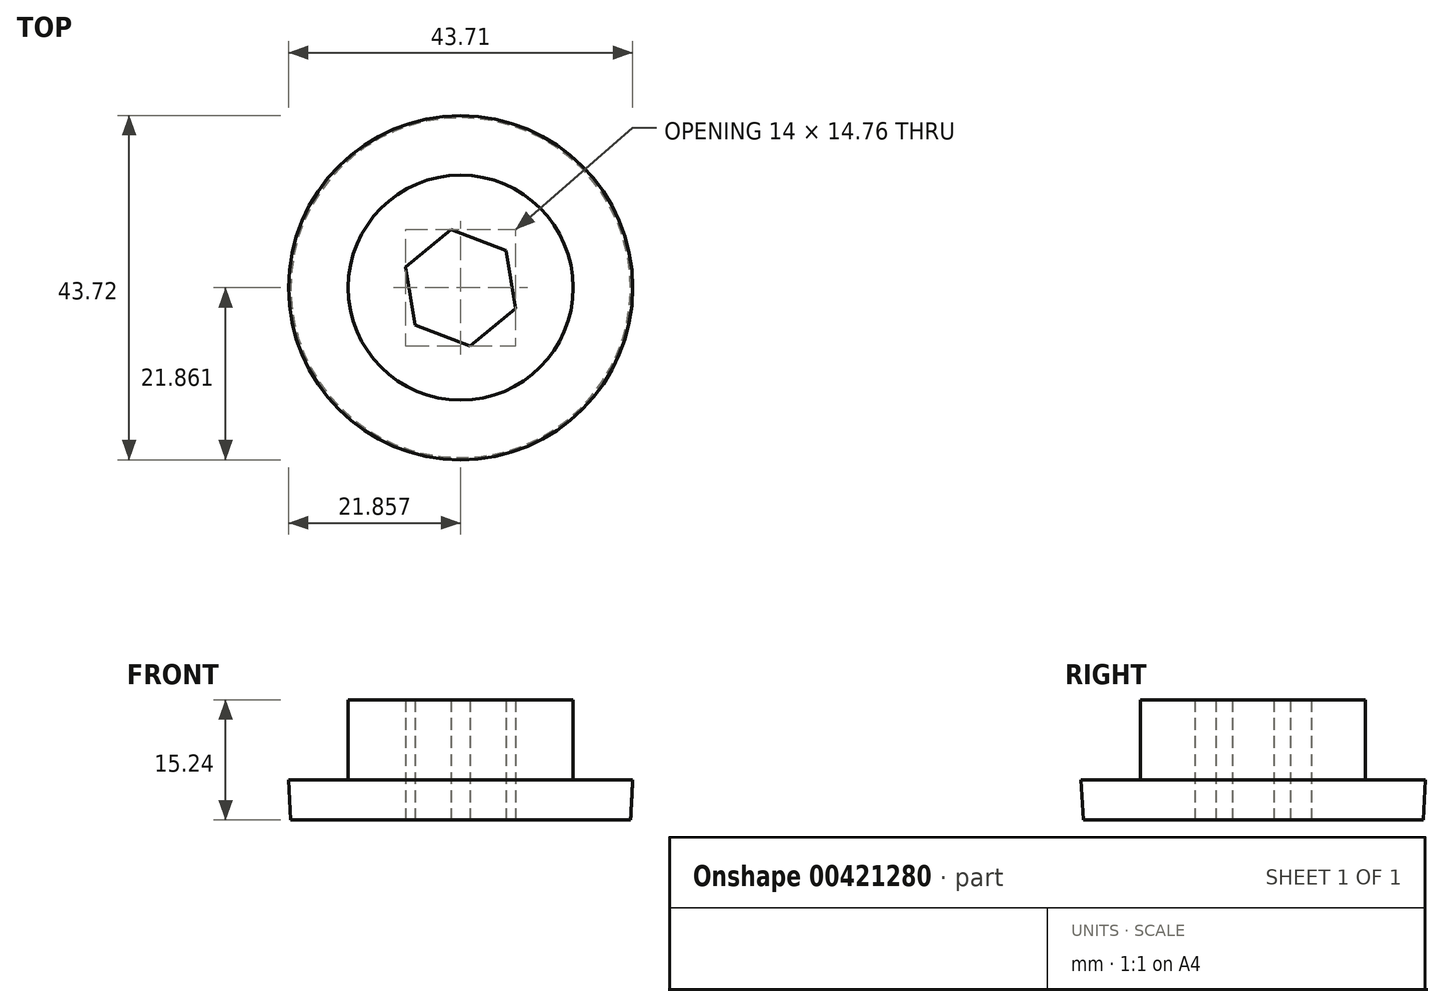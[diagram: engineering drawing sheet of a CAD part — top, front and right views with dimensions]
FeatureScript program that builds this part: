
annotation { "Feature Type Name" : "Feature", "Feature Type Description" : "" }
export const myFeature = defineFeature(function(context is Context, id is Id, definition is map)
    precondition{}
    {
        {
            var Q0;
            Q0=qCreatedBy(makeId("Top.planeOp"),FACE);
            var sketch = newSketch(context, id + "F0", { "sketchPlane" : qUnion([Q0])});
            skCircle(sketch, "E0", {"center": v(-39.13, 30.98) * mm, "radius": 21.59 * mm});
            skCircle(sketch, "E1", {"center": v(-39.13, 30.98) * mm, "radius": 14.29 * mm});
            skCircle(sketch, "E2.cCircle", {"center": v(-39.13, 30.98) * mm, "radius": 7.48 * mm, "construction": true});
            skLineSegment(sketch, "E2.0", {"start": v(-33.36, 35.73) * mm, "end": v(-32.13, 28.35) * mm});
            skLineSegment(sketch, "E2.1", {"start": v(-32.13, 28.35) * mm, "end": v(-37.9, 23.6) * mm});
            skLineSegment(sketch, "E2.2", {"start": v(-37.9, 23.6) * mm, "end": v(-44.9, 26.23) * mm});
            skLineSegment(sketch, "E2.3", {"start": v(-44.9, 26.23) * mm, "end": v(-46.13, 33.6) * mm});
            skLineSegment(sketch, "E2.4", {"start": v(-46.13, 33.6) * mm, "end": v(-40.36, 38.36) * mm});
            skLineSegment(sketch, "E2.5", {"start": v(-40.36, 38.36) * mm, "end": v(-33.36, 35.73) * mm});
            skSolve(sketch);
        }
        {
            var Q0;
            Q0=makeQuery(id+"F0.imprint","IMPRINT",FACE,{"disambiguationData":[TD([[makeQuery(id+"F0.imprint","IMPRINT",EDGE,{"derivedFrom":sQuery(id+"F0.wireOp",EDGE,"E0")}),1.0]])]});
            extrude(context, id + "F1", {"entities" : qUnion([Q0]), "depth" : 5.08 * mm, "hasDraft" : true, "draftAngle" : 3 * degree});
        }
        {
            var Q0;
            Q0=makeQuery(id+"F0.imprint","IMPRINT",FACE,{"disambiguationData":[TD([[makeQuery(id+"F0.imprint","IMPRINT",EDGE,{"derivedFrom":sQuery(id+"F0.wireOp",EDGE,"E1")}),1.0]])]});
            extrude(context, id + "F2", {"entities" : qUnion([Q0]), "operationType" : NewBodyOperationType.ADD, "depth" : 15.24 * mm});
        }
    });
